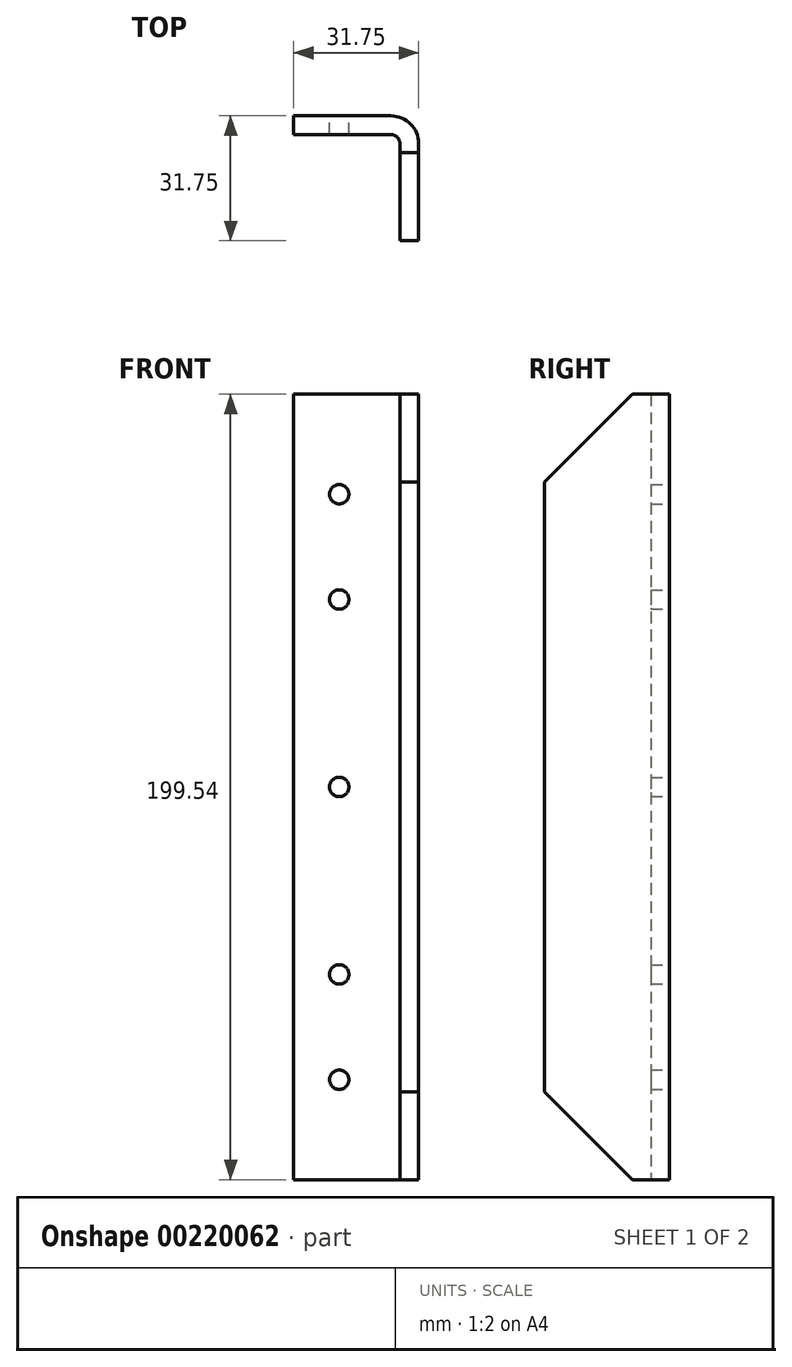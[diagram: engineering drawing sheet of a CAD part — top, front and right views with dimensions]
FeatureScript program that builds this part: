
annotation { "Feature Type Name" : "Feature", "Feature Type Description" : "" }
export const myFeature = defineFeature(function(context is Context, id is Id, definition is map)
    precondition{}
    {
        {
            var Q0;
            Q0=qCreatedBy(makeId("Top.planeOp"),FACE);
            var sketch = newSketch(context, id + "F0", { "sketchPlane" : qUnion([Q0])});
            skLineSegment(sketch, "E0", {"start": v(0, -7.06) * mm, "end": v(0, -31.75) * mm});
            skLineSegment(sketch, "E1", {"start": v(-7.06, 0) * mm, "end": v(-31.75, 0) * mm});
            skLineSegment(sketch, "E2", {"start": v(-31.75, 0) * mm, "end": v(-31.75, -4.78) * mm});
            skLineSegment(sketch, "E3", {"start": v(-31.75, -4.78) * mm, "end": v(-7.06, -4.78) * mm});
            skLineSegment(sketch, "E4", {"start": v(-4.78, -7.06) * mm, "end": v(-4.78, -31.75) * mm});
            skLineSegment(sketch, "E5", {"start": v(-4.78, -31.75) * mm, "end": v(0, -31.75) * mm});
            skPoint(sketch, "E6.visualSharp", {"position": v(-4.78, -4.78) * mm});
            skArc(sketch, "E6.filletArc", {"start": v(-4.78, -7.06) * mm, "mid": v(-5.44, -5.44) * mm, "end": v(-7.06, -4.78) * mm});
            skPoint(sketch, "E7.visualSharp", {"position": v(0, 0) * mm});
            skArc(sketch, "E7.filletArc", {"start": v(0, -7.06) * mm, "mid": v(-2.07, -2.07) * mm, "end": v(-7.06, 0) * mm});
            skSolve(sketch);
        }
        {
            var Q0;
            Q0 = qSketchRegion(id + "F0", true);
            extrude(context, id + "F1", {"entities" : qUnion([Q0]), "depth" : 199.54 * mm});
        }
        {
            var Q0;
            Q0=makeQuery(id+"F1.opExtrude","CAP_EDGE",EDGE,{"disambiguationData":[OSD([sQuery(id+"F0.wireOp",EDGE,"E5")])],"isStart":false});
            var Q1;
            Q1=makeQuery(id+"F1.opExtrude","CAP_EDGE",EDGE,{"disambiguationData":[OSD([sQuery(id+"F0.wireOp",EDGE,"E5")])],"isStart":true});
            chamfer(context, id + "F2", {"entities" : qUnion([Q0, Q1]), "width" : 22.35 * mm, "tangentPropagation" : true});
        }
        {
            var Q0;
            Q0=qCreatedBy(makeId("Front.planeOp"),FACE);
            var sketch = newSketch(context, id + "F3", { "sketchPlane" : qUnion([Q0])});
            skLineSegment(sketch, "E8.0", {"start": v(0, 199.54) * mm, "end": v(0, 0) * mm, "construction": true});
            skLineSegment(sketch, "E9", {"start": v(-20.2, 199.54) * mm, "end": v(-20.2, 0) * mm, "construction": true});
            skLineSegment(sketch, "E10.0", {"start": v(-7.06, 199.54) * mm, "end": v(-31.75, 199.54) * mm, "construction": true});
            skLineSegment(sketch, "E11.0", {"start": v(-7.06, 0) * mm, "end": v(-31.75, 0) * mm, "construction": true});
            skCircle(sketch, "E12", {"center": v(-20.2, 174.14) * mm, "radius": 2.46 * mm});
            skCircle(sketch, "E13", {"center": v(-20.2, 99.77) * mm, "radius": 2.46 * mm});
            skCircle(sketch, "E14", {"center": v(-20.2, 25.4) * mm, "radius": 2.46 * mm});
            skCircle(sketch, "E15", {"center": v(-20.2, 147.4) * mm, "radius": 2.46 * mm});
            skCircle(sketch, "E16", {"center": v(-20.2, 52.15) * mm, "radius": 2.46 * mm});
            skSolve(sketch);
        }
        {
            var Q0;
            Q0 = qSketchRegion(id + "F3", true);
            extrude(context, id + "F4", {"entities" : qUnion([Q0]), "operationType" : NewBodyOperationType.REMOVE, "depth" : 25.4 * mm});
        }
    });
